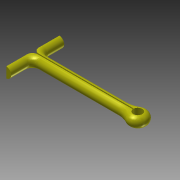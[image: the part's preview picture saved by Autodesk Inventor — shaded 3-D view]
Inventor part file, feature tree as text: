
AUTODESK INVENTOR PART (.ipt)
format: ipt  version: 2015 (Build 190159000, 159)  size: 176,640 bytes
history: native  units: mm
features: fillet x2, extrude x1, sketch x1
ambient origin geometry x8: Origin, YZ Plane, XZ Plane, XY Plane, X Axis, Y Axis, Z Axis, Center Point
bodies: 实体1 (feature_tree)
feature tree (4):
  extrude  "拉伸1"  Depth=1.75mm
  fillet  "圆角1"  Radius=2.0mm
  fillet  "圆角2"  Radius=4.0mm
  sketch  "草图1"  dims[d0=5.186385mm d1=1.75mm d4=2.0mm d5=4.0mm d6=4.0mm d7=4.0mm d8=16.0mm d9=0.9mm d10=4.9mm d11=4.9mm d12=0.85mm d13=2.0mm d14=0.0mm d15=1.0mm d16=1.0mm]
